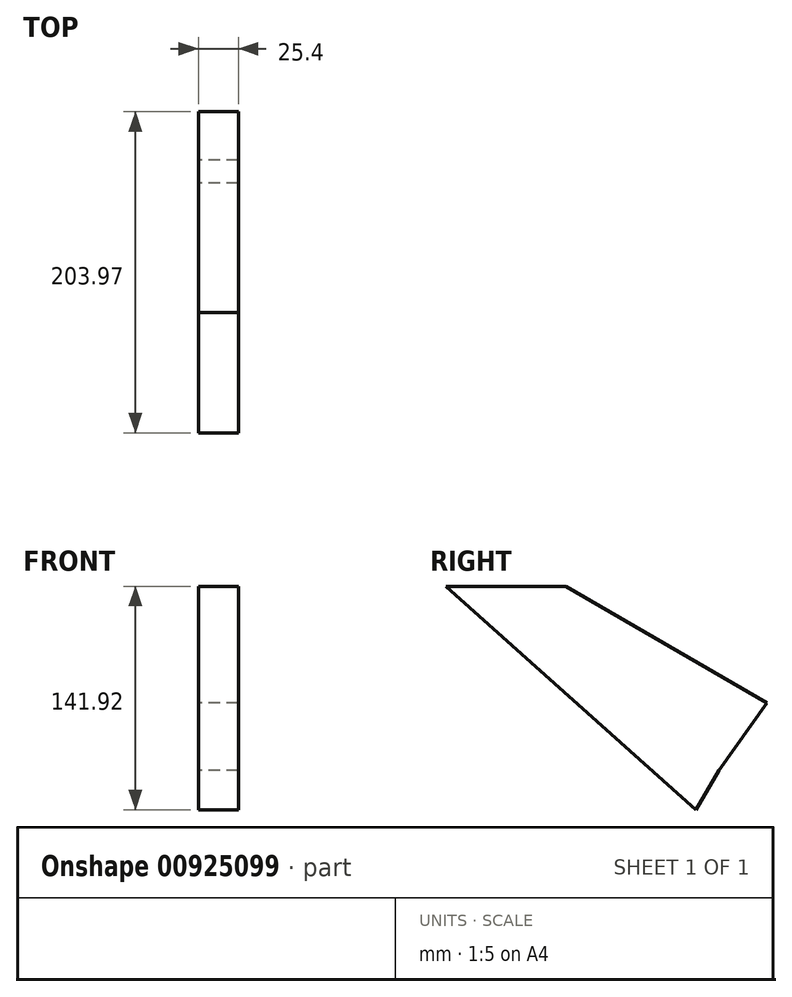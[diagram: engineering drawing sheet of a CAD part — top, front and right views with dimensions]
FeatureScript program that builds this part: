
annotation { "Feature Type Name" : "Feature", "Feature Type Description" : "" }
export const myFeature = defineFeature(function(context is Context, id is Id, definition is map)
    precondition{}
    {
        {
            var Q0;
            Q0=qCreatedBy(makeId("Right.planeOp"),FACE);
            var sketch = newSketch(context, id + "F0", { "sketchPlane" : qUnion([Q0])});
            skLineSegment(sketch, "E0", {"start": v(0, 0) * mm, "end": v(127.65, -74.15) * mm});
            skLineSegment(sketch, "E1", {"start": v(127.65, -74.15) * mm, "end": v(-76.32, 0) * mm});
            skLineSegment(sketch, "E2", {"start": v(-76.32, 0) * mm, "end": v(0, 0) * mm});
            skLineSegment(sketch, "E3", {"start": v(96.97, -116.8) * mm, "end": v(82.38, -141.92) * mm});
            skLineSegment(sketch, "E4", {"start": v(82.38, -141.92) * mm, "end": v(-76.32, 0) * mm});
            skLineSegment(sketch, "E5", {"start": v(127.65, -74.15) * mm, "end": v(96.97, -116.8) * mm});
            skSolve(sketch);
        }
        {
            var Q0;
            Q0 = qSketchRegion(id + "F0", true);
            extrude(context, id + "F1", {"entities" : qUnion([Q0]), "depth" : 25.4 * mm, "offsetDistance" : 25.4 * mm});
        }
    });
